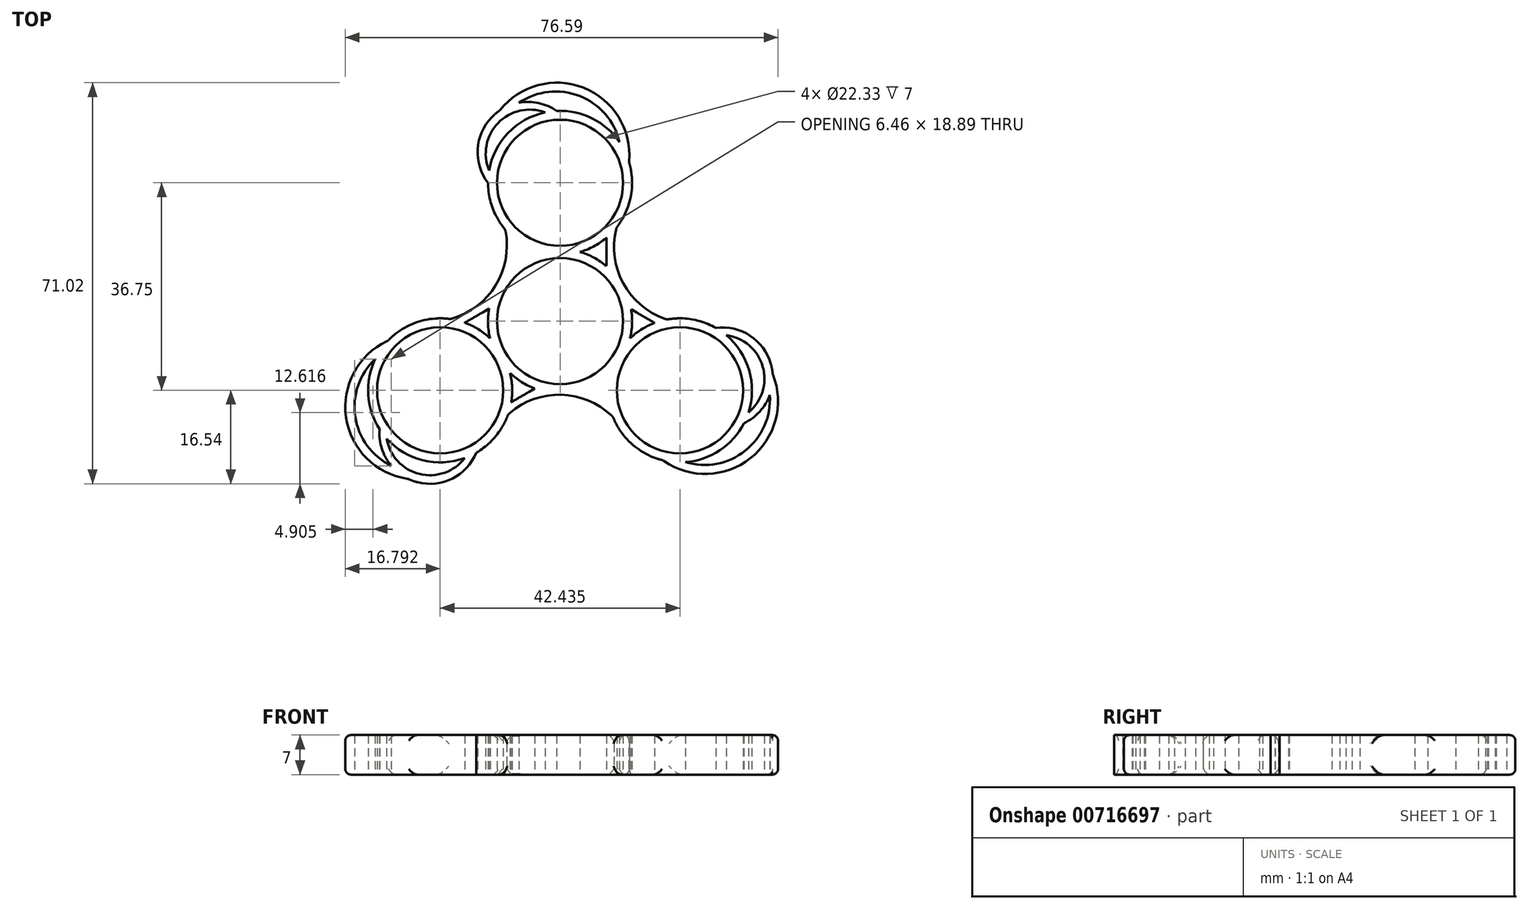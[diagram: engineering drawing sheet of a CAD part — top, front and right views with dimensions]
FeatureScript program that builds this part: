
annotation { "Feature Type Name" : "Feature", "Feature Type Description" : "" }
export const myFeature = defineFeature(function(context is Context, id is Id, definition is map)
    precondition{}
    {
        {
            var Q0;
            Q0=qCreatedBy(makeId("Top.planeOp"),FACE);
            var sketch = newSketch(context, id + "F0", { "sketchPlane" : qUnion([Q0])});
            skCircle(sketch, "E0", {"center": v(0, 0) * mm, "radius": 11.16 * mm});
            skCircle(sketch, "E1", {"center": v(0, 0) * mm, "radius": 12.75 * mm});
            skCircle(sketch, "E2", {"center": v(0, 24.5) * mm, "radius": 11.16 * mm});
            skCircle(sketch, "E3", {"center": v(0, 24.5) * mm, "radius": 12.75 * mm});
            skCircle(sketch, "E4.1.0", {"center": v(-21.22, -12.25) * mm, "radius": 11.16 * mm});
            skCircle(sketch, "E4.1.1", {"center": v(-21.22, -12.25) * mm, "radius": 12.75 * mm});
            skCircle(sketch, "E4.2.0", {"center": v(21.22, -12.25) * mm, "radius": 11.16 * mm});
            skCircle(sketch, "E4.2.1", {"center": v(21.22, -12.25) * mm, "radius": 12.75 * mm});
            skArc(sketch, "E5", {"start": v(-0.62, 37.24) * mm, "mid": v(-12.15, 36.04) * mm, "end": v(-12.75, 24.46) * mm});
            skArc(sketch, "E6", {"start": v(-2.66, 36.97) * mm, "mid": v(-10.98, 35.08) * mm, "end": v(-12.56, 26.7) * mm});
            skArc(sketch, "E7.1.0", {"start": v(-31.94, -19.15) * mm, "mid": v(-25.14, -28.55) * mm, "end": v(-14.8, -23.27) * mm});
            skArc(sketch, "E7.1.1", {"start": v(-30.69, -20.79) * mm, "mid": v(-24.9, -27.05) * mm, "end": v(-16.84, -24.23) * mm});
            skArc(sketch, "E7.2.0", {"start": v(32.55, -18.08) * mm, "mid": v(37.3, -7.5) * mm, "end": v(27.56, -1.19) * mm});
            skArc(sketch, "E7.2.1", {"start": v(33.35, -16.18) * mm, "mid": v(35.87, -8.03) * mm, "end": v(29.4, -2.47) * mm});
            skArc(sketch, "E8", {"start": v(12.22, 28.13) * mm, "mid": v(4.18, 41.32) * mm, "end": v(-10.72, 37.26) * mm});
            skArc(sketch, "E9", {"start": v(10.53, 31.7) * mm, "mid": v(3.48, 39.86) * mm, "end": v(-7.25, 38.68) * mm});
            skArc(sketch, "E10.1.0", {"start": v(-32.7, -6.73) * mm, "mid": v(-36.26, -16.92) * mm, "end": v(-29.87, -25.62) * mm});
            skArc(sketch, "E10.1.1", {"start": v(-30.47, -3.48) * mm, "mid": v(-37.87, -17.04) * mm, "end": v(-26.9, -27.92) * mm});
            skArc(sketch, "E10.2.0", {"start": v(22.18, -24.96) * mm, "mid": v(32.78, -22.94) * mm, "end": v(37.12, -13.06) * mm});
            skArc(sketch, "E10.2.1", {"start": v(18.25, -24.65) * mm, "mid": v(33.7, -24.28) * mm, "end": v(37.63, -9.34) * mm});
            skArc(sketch, "E11", {"start": v(-19.38, 0.37) * mm, "mid": v(-11.37, 6.37) * mm, "end": v(-9.72, 16.25) * mm});
            skArc(sketch, "E12.1.0", {"start": v(9.37, -16.97) * mm, "mid": v(0.17, -13.03) * mm, "end": v(-9.21, -16.54) * mm});
            skArc(sketch, "E12.2.0", {"start": v(10.01, 16.6) * mm, "mid": v(11.2, 6.66) * mm, "end": v(18.93, 0.3) * mm});
            skLineSegment(sketch, "E13", {"start": v(8.19, 14.73) * mm, "end": v(8.19, 9.77) * mm});
            skLineSegment(sketch, "E14", {"start": v(-8.1, 14.66) * mm, "end": v(-8.1, 9.84) * mm});
            skLineSegment(sketch, "E15.1.0", {"start": v(-8.64, -14.35) * mm, "end": v(-4.47, -11.94) * mm});
            skLineSegment(sketch, "E15.1.1", {"start": v(-16.85, -0.27) * mm, "end": v(-12.56, 2.2) * mm});
            skLineSegment(sketch, "E15.2.0", {"start": v(16.74, -0.31) * mm, "end": v(12.58, 2.1) * mm});
            skLineSegment(sketch, "E15.2.1", {"start": v(8.66, -14.46) * mm, "end": v(4.37, -11.98) * mm});
            skSolve(sketch);
        }
        {
            var Q0;
            {var subQ0=sQuery(id+"F0.wireOp",EDGE,"E12.2.0");Q0=makeQuery(id+"F0.imprint","IMPRINT",FACE,{"disambiguationData":[TD([[makeQuery(id+"F0.imprint","IMPRINT",EDGE,{"derivedFrom":subQ0}),-1.0]])]});}
            var Q1;
            {var subQ0=sQuery(id+"F0.wireOp",EDGE,"E11");Q1=makeQuery(id+"F0.imprint","IMPRINT",FACE,{"disambiguationData":[TD([[makeQuery(id+"F0.imprint","IMPRINT",EDGE,{"derivedFrom":subQ0}),-1.0]])]});}
            var Q2;
            Q2=makeQuery(id+"F0.imprint","IMPRINT",FACE,{"disambiguationData":[TD([[makeQuery(id+"F0.imprint","IMPRINT",EDGE,{"derivedFrom":sQuery(id+"F0.wireOp",EDGE,"E0")}),-1.0]])]});
            var Q3;
            Q3=makeQuery(id+"F0.imprint","IMPRINT",FACE,{"disambiguationData":[TD([[makeQuery(id+"F0.imprint","IMPRINT",EDGE,{"derivedFrom":sQuery(id+"F0.wireOp",EDGE,"E2")}),-1.0]])]});
            var Q4;
            {var subQ6=sQuery(id+"F0.wireOp",EDGE,"E6");Q4=makeQuery(id+"F0.imprint","IMPRINT",FACE,{"disambiguationData":[TD([[makeQuery(id+"F0.imprint","IMPRINT",EDGE,{"derivedFrom":subQ6}),-1.0]])]});}
            var Q5;
            {var subQ0=sQuery(id+"F0.wireOp",EDGE,"E8");Q5=makeQuery(id+"F0.imprint","IMPRINT",FACE,{"disambiguationData":[TD([[makeQuery(id+"F0.imprint","IMPRINT",EDGE,{"derivedFrom":subQ0}),1.0]])]});}
            var Q6;
            Q6=makeQuery(id+"F0.imprint","IMPRINT",FACE,{"disambiguationData":[TD([[makeQuery(id+"F0.imprint","IMPRINT",EDGE,{"derivedFrom":sQuery(id+"F0.wireOp",EDGE,"E4.2.0")}),-1.0]])]});
            var Q7;
            {var subQ6=sQuery(id+"F0.wireOp",EDGE,"E7.2.1");Q7=makeQuery(id+"F0.imprint","IMPRINT",FACE,{"disambiguationData":[TD([[makeQuery(id+"F0.imprint","IMPRINT",EDGE,{"derivedFrom":subQ6}),-1.0]])]});}
            var Q8;
            {var subQ0=sQuery(id+"F0.wireOp",EDGE,"E12.1.0");Q8=makeQuery(id+"F0.imprint","IMPRINT",FACE,{"disambiguationData":[TD([[makeQuery(id+"F0.imprint","IMPRINT",EDGE,{"derivedFrom":subQ0}),-1.0]])]});}
            var Q9;
            {var subQ0=sQuery(id+"F0.wireOp",EDGE,"E10.2.0");Q9=makeQuery(id+"F0.imprint","IMPRINT",FACE,{"disambiguationData":[TD([[makeQuery(id+"F0.imprint","IMPRINT",EDGE,{"derivedFrom":subQ0}),-1.0]])]});}
            var Q10;
            Q10=makeQuery(id+"F0.imprint","IMPRINT",FACE,{"disambiguationData":[TD([[makeQuery(id+"F0.imprint","IMPRINT",EDGE,{"derivedFrom":sQuery(id+"F0.wireOp",EDGE,"E4.1.0")}),-1.0]])]});
            var Q11;
            {var subQ6=sQuery(id+"F0.wireOp",EDGE,"E7.1.1");Q11=makeQuery(id+"F0.imprint","IMPRINT",FACE,{"disambiguationData":[TD([[makeQuery(id+"F0.imprint","IMPRINT",EDGE,{"derivedFrom":subQ6}),-1.0]])]});}
            var Q12;
            {var subQ0=sQuery(id+"F0.wireOp",EDGE,"E10.1.0");Q12=makeQuery(id+"F0.imprint","IMPRINT",FACE,{"disambiguationData":[TD([[makeQuery(id+"F0.imprint","IMPRINT",EDGE,{"derivedFrom":subQ0}),-1.0]])]});}
            var Q13;
            {var subQ0=sQuery(id+"F0.wireOp",EDGE,"E3");var subQ1=sQuery(id+"F0.wireOp",EDGE,"E1");var subQ2=makeQuery(id+"F0.imprint","INTERSECT",VERTEX,{"disambiguationData":[OD(0.0)],"derivedFrom":[subQ1,subQ0]});Q13=makeQuery(id+"F0.imprint","IMPRINT",FACE,{"disambiguationData":[TD([[makeQuery(id+"F0.imprint","IMPRINT",EDGE,{"disambiguationData":[TD([[subQ2,-1.0]])],"derivedFrom":subQ1}),1.0]])]});}
            var Q14;
            {var subQ0=sQuery(id+"F0.wireOp",EDGE,"E4.2.1");var subQ1=sQuery(id+"F0.wireOp",EDGE,"E1");var subQ2=makeQuery(id+"F0.imprint","INTERSECT",VERTEX,{"disambiguationData":[OD(0.0)],"derivedFrom":[subQ1,subQ0]});Q14=makeQuery(id+"F0.imprint","IMPRINT",FACE,{"disambiguationData":[TD([[makeQuery(id+"F0.imprint","IMPRINT",EDGE,{"disambiguationData":[TD([[subQ2,-1.0]])],"derivedFrom":subQ1}),1.0]])]});}
            var Q15;
            {var subQ0=sQuery(id+"F0.wireOp",EDGE,"E4.1.1");var subQ1=sQuery(id+"F0.wireOp",EDGE,"E1");var subQ2=makeQuery(id+"F0.imprint","INTERSECT",VERTEX,{"disambiguationData":[OD(0.0)],"derivedFrom":[subQ1,subQ0]});Q15=makeQuery(id+"F0.imprint","IMPRINT",FACE,{"disambiguationData":[TD([[makeQuery(id+"F0.imprint","IMPRINT",EDGE,{"disambiguationData":[TD([[subQ2,-1.0]])],"derivedFrom":subQ1}),1.0]])]});}
            var Q16;
            {var subQ0=sQuery(id+"F0.wireOp",EDGE,"E14");Q16=makeQuery(id+"F0.imprint","IMPRINT",FACE,{"disambiguationData":[TD([[makeQuery(id+"F0.imprint","IMPRINT",EDGE,{"derivedFrom":subQ0}),1.0]])]});}
            var Q17;
            {var subQ0=sQuery(id+"F0.wireOp",EDGE,"E15.2.1");Q17=makeQuery(id+"F0.imprint","IMPRINT",FACE,{"disambiguationData":[TD([[makeQuery(id+"F0.imprint","IMPRINT",EDGE,{"derivedFrom":subQ0}),-1.0]])]});}
            extrude(context, id + "F1", {"entities" : qUnion([Q0, Q1, Q2, Q3, Q4, Q5, Q6, Q7, Q8, Q9, Q10, Q11, Q12, Q13, Q14, Q15, Q16, Q17]), "depth" : 7 * mm, "offsetDistance" : 25 * mm});
        }
        {
            var Q0;
            Q0=makeQuery(id+"F1.opExtrude","SWEPT_FACE",FACE,{"disambiguationData":[OSD([sQuery(id+"F0.wireOp",EDGE,"E12.1.0")])]});
            var Q1;
            Q1=makeQuery(id+"F1.opExtrude","SWEPT_FACE",FACE,{"disambiguationData":[OSD([sQuery(id+"F0.wireOp",EDGE,"E12.2.0")])]});
            var Q2;
            Q2=makeQuery(id+"F1.opExtrude","SWEPT_FACE",FACE,{"disambiguationData":[OSD([sQuery(id+"F0.wireOp",EDGE,"E11")])]});
            fillet(context, id + "F2", {"entities" : qUnion([Q0, Q1, Q2]), "radius" : 1.5 * mm, "tangentPropagation" : true, "allowEdgeOverflow" : false});
        }
        {
            var Q0;
            Q0=makeQuery(id+"F1.opExtrude","SWEPT_FACE",FACE,{"disambiguationData":[OSD([sQuery(id+"F0.wireOp",EDGE,"E10.1.1")])]});
            var Q1;
            Q1=makeQuery(id+"F1.opExtrude","SWEPT_FACE",FACE,{"disambiguationData":[OSD([sQuery(id+"F0.wireOp",EDGE,"E10.2.1")])]});
            var Q2;
            Q2=makeQuery(id+"F1.opExtrude","SWEPT_FACE",FACE,{"disambiguationData":[OSD([sQuery(id+"F0.wireOp",EDGE,"E8")])]});
            fillet(context, id + "F3", {"entities" : qUnion([Q0, Q1, Q2]), "radius" : 1 * mm, "tangentPropagation" : true, "allowEdgeOverflow" : false});
        }
    });
